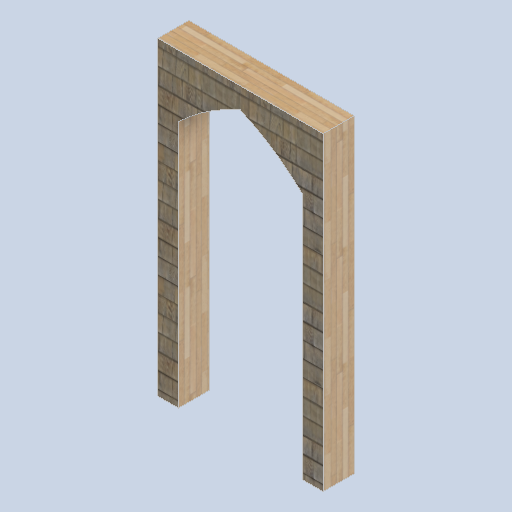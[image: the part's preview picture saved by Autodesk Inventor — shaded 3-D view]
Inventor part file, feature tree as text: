
AUTODESK INVENTOR PART (.ipt)
format: ipt  version: 2024.2 (Build 282272000, 272)  size: 209,920 bytes
history: native  units: mm
features: extrude x2, sketch x2
ambient origin geometry x8: Origin, YZ Plane, XZ Plane, XY Plane, X Axis, Y Axis, Z Axis, Center Point
bodies: Solid1 (feature_tree)
feature tree (4):
  extrude  "Extrusion1"  Depth=2000.0mm
  extrude  "Extrusion2"  TaperAngle=0.0deg  [1 undecoded]
  sketch  "Sketch1"  dims[d0=300.0mm d1=0.0mm d8=2000.0mm]
  sketch  "Sketch2"  dims[d9=2000.0mm d10=0.0mm d11=0.0mm d6=500.0mm d7=0.872665mm]
note: 1 required parameter value undecoded (feature->parameter linkage not recoverable at this tier; creation-order binding heuristic only, values carry confidence <= 0.55)
